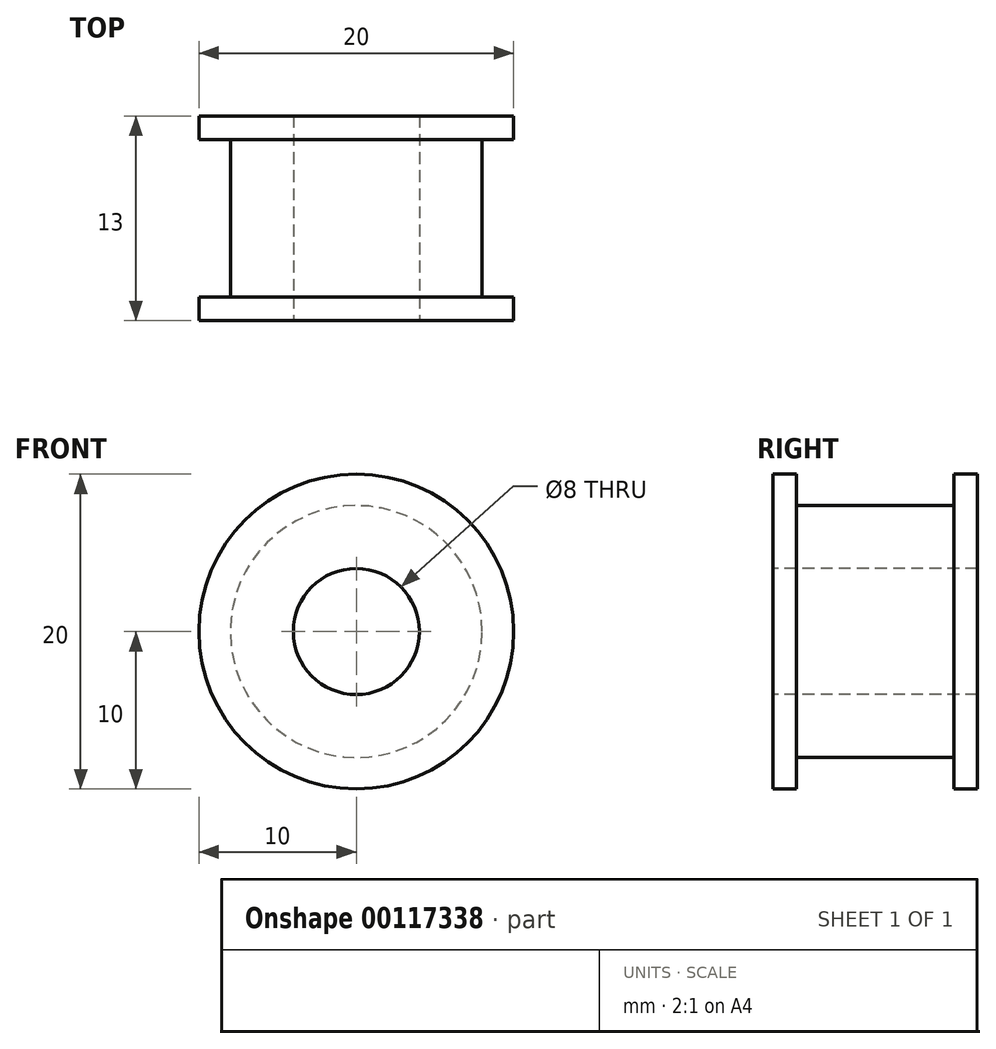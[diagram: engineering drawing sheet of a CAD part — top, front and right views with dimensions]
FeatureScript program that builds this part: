
annotation { "Feature Type Name" : "Feature", "Feature Type Description" : "" }
export const myFeature = defineFeature(function(context is Context, id is Id, definition is map)
    precondition{}
    {
        {
            var Q0;
            Q0=qCreatedBy(makeId("Front.planeOp"),FACE);
            var sketch = newSketch(context, id + "F0", { "sketchPlane" : qUnion([Q0])});
            skCircle(sketch, "E0", {"center": v(0, 0) * mm, "radius": 10 * mm});
            skSolve(sketch);
        }
        {
            var Q0;
            Q0=qSketchRegion(id+"F0",true);
            extrude(context, id + "F1", {"entities" : qUnion([Q0]), "depth" : 1.5 * mm});
        }
        {
            var Q0;
            Q0=makeQuery(id+"F1.opExtrude","CAP_FACE",FACE,{"disambiguationData":[OSD([sQuery(id+"F0.wireOp",EDGE,"E0")])],"isStart":false});
            var sketch = newSketch(context, id + "F2", { "sketchPlane" : qUnion([Q0])});
            skCircle(sketch, "E1", {"center": v(0, 0) * mm, "radius": 8 * mm});
            skSolve(sketch);
        }
        {
            var Q0;
            Q0=qSketchRegion(id+"F2",true);
            extrude(context, id + "F3", {"entities" : qUnion([Q0]), "operationType" : NewBodyOperationType.ADD, "depth" : 10 * mm});
        }
        {
            var Q0;
            Q0=makeQuery(id+"F3.opExtrude","CAP_FACE",FACE,{"disambiguationData":[OSD([sQuery(id+"F2.wireOp",EDGE,"E1")])],"isStart":false});
            var sketch = newSketch(context, id + "F4", { "sketchPlane" : qUnion([Q0])});
            skCircle(sketch, "E2", {"center": v(0, 0) * mm, "radius": 10 * mm});
            skSolve(sketch);
        }
        {
            var Q0;
            Q0=qSketchRegion(id+"F4",true);
            extrude(context, id + "F5", {"entities" : qUnion([Q0]), "operationType" : NewBodyOperationType.ADD, "depth" : 1.5 * mm});
        }
        {
            var Q0;
            Q0=makeQuery(id+"F5.opExtrude","CAP_FACE",FACE,{"disambiguationData":[OSD([sQuery(id+"F4.wireOp",EDGE,"E2")])],"isStart":false});
            var sketch = newSketch(context, id + "F6", { "sketchPlane" : qUnion([Q0])});
            skCircle(sketch, "E3", {"center": v(0, 0) * mm, "radius": 4 * mm});
            skSolve(sketch);
        }
        {
            var Q0;
            Q0=makeQuery(id+"F6.imprint","IMPRINT",FACE,{"disambiguationData":[TD([[makeQuery(id+"F6.imprint","IMPRINT",EDGE,{"derivedFrom":sQuery(id+"F6.wireOp",EDGE,"E3")}),1.0]])]});
            extrude(context, id + "F7", {"entities" : qUnion([Q0]), "operationType" : NewBodyOperationType.REMOVE, "oppositeDirection" : true, "depth" : 25 * mm});
        }
    });
